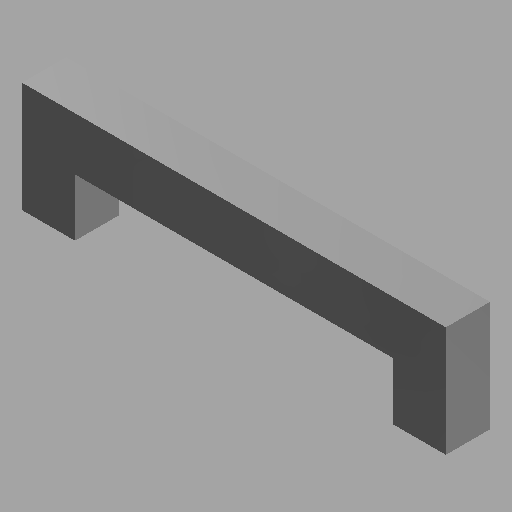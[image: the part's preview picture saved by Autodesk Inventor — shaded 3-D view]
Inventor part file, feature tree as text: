
AUTODESK INVENTOR PART (.ipt)
format: ipt  version: 2023 (Build 270158030, 158C)  size: 94,208 bytes
history: native  units: mm (DEFAULTED — no unit token found)
features: other x1, extrude x1, sketch x1
ambient origin geometry x8: Origin, YZ Plane, XZ Plane, XY Plane, X Axis, Y Axis, Z Axis, Center Point
bodies: Solid1 (feature_tree)
feature tree (3):
  other  "Block header 2"
  extrude  "Extrusion1"  Depth=165.1mm
  sketch  "Sketch1"  dims[d0=914.4mm d1=165.1mm d2=25.4mm d3=0.0mm]
